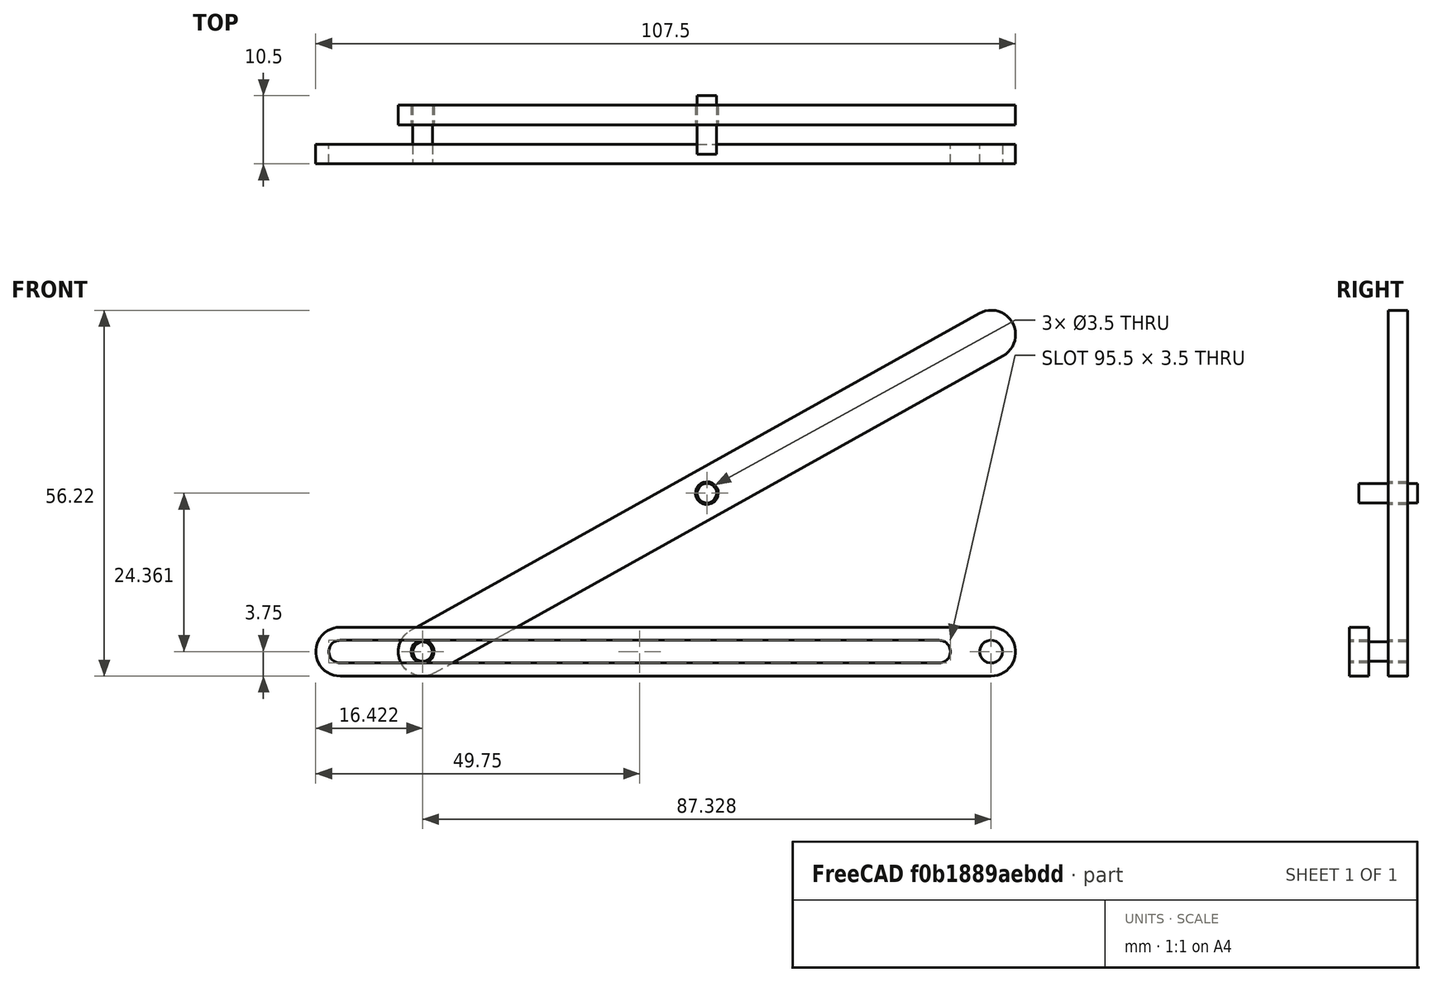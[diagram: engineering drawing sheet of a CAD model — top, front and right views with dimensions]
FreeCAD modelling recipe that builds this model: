
FCSTD DOCUMENT  (FreeCAD 1.0R38643 (Git))
Label: scissor_lift
License: All rights reserved
LicenseURL: http://en.wikipedia.org/wiki/All_rights_reserved
objects: App::FeaturePython×8, PartDesign::Body×6, Sketcher::SketchObject×3, PartDesign::Pad×3, PartDesign::FeatureBase×3, PartDesign::SubShapeBinder×1, Assembly::JointGroup×1, Assembly::AssemblyObject×1
note: 28 computed .brp shape members not serialized (recipe doc carries the construction recipe); baked Part::Feature solids carry a one-line shape summary decoded from their .brp

FEATURE [Sketcher::SketchObject] Sketch
  ArcFitTolerance = 1e-06
  AttachmentSupport = -> [XY_Plane]
  FullyConstrained = true
  MakeInternals = false
  MapMode = 5
  sketch-geometry (9):
    g0: ArcOfCircle CenterX=-50 CenterY=0 CenterZ=0 NormalX=0 NormalY=0 NormalZ=1 AngleXU=0 Radius=3.75 StartAngle=1.5708 EndAngle=4.71239
    g1: ArcOfCircle CenterX=50 CenterY=0 CenterZ=0 NormalX=0 NormalY=0 NormalZ=1 AngleXU=0 Radius=3.75 StartAngle=4.71239 EndAngle=7.85398
    g2: LineSegment StartX=-50 StartY=3.75 StartZ=0 EndX=50 EndY=3.75 EndZ=0
    g3: LineSegment StartX=-50 StartY=-3.75 StartZ=0 EndX=50 EndY=-3.75 EndZ=0
    g4: ArcOfCircle CenterX=-50 CenterY=0 CenterZ=0 NormalX=0 NormalY=0 NormalZ=1 AngleXU=0 Radius=1.75 StartAngle=1.5708 EndAngle=4.71239
    g5: ArcOfCircle CenterX=42 CenterY=1.1702e-12 CenterZ=0 NormalX=0 NormalY=0 NormalZ=1 AngleXU=0 Radius=1.75 StartAngle=4.71239 EndAngle=7.85398
    g6: LineSegment StartX=-50 StartY=1.75 StartZ=0 EndX=42 EndY=1.75 EndZ=0
    g7: LineSegment StartX=-50 StartY=-1.75 StartZ=0 EndX=42 EndY=-1.75 EndZ=0
    g8: Circle CenterX=50 CenterY=0 CenterZ=0 NormalX=0 NormalY=0 NormalZ=1 AngleXU=0 Radius=1.75
  constraints (20):
    c: Tangent(g0,g2) = 1.5708
    c: Tangent(g0,g3) = -1.5708
    c: Tangent(g1,g2) = 1.5708
    c: Tangent(g1,g3) = -1.5708
    c: Equal(g0,g1)
    c: PointOnObject(g0,g-1)
    c: Symmetric(g0,g1,g-1)
    c: DistanceX(g0,g1) = 100
    c: DistanceY(g0,g0) = 7.5
    c: Tangent(g4,g6) = 1.5708
    c: Tangent(g4,g7) = -1.5708
    c: Tangent(g5,g6) = 1.5708
    c: Tangent(g5,g7) = -1.5708
    c: Equal(g4,g5)
    c: Horizontal(g7)
    c: Coincident(g4,g0)
    c: Distance(g4,g4) = 3.5
    c: Coincident(g8,g1)
    c: Diameter(g8) = 3.5
    c: DistanceX(g5,g1) = 8
FEATURE [PartDesign::Pad] Pad
  Direction = (0,0,1)
  Length = 3
  Length2 = 10
  Profile = -> Sketch
  ReferenceAxis = -> Sketch [N_Axis]
  Suppressed = false
  Type = 0
FEATURE [PartDesign::Body] Body  label="base"
  AllowCompound = false
  Group = -> [Sketch,Pad]
  Origin = -> Origin
  Placement = pos=(0,1.5,1.5) rot=(1,0,0;1.5708rad)
  Tip = -> Pad
FEATURE [PartDesign::SubShapeBinder] Binder
  BindCopyOnChange = 0
  BindMode = 0
  ClaimChildren = false
  Context = -> Body001 [Binder.]
  Fuse = false
  MakeFace = true
  OffsetFill = false
  OffsetIntersection = false
  OffsetJoinType = 0
  OffsetOpenResult = false
  PartialLoad = false
  Relative = true
  Support = -> [Body]
  _Version = 2
FEATURE [Sketcher::SketchObject] Sketch001
  ArcFitTolerance = 1e-06
  AttachmentSupport = -> [XY_Plane001]
  ExternalGeometry = -> [Binder]
  FullyConstrained = true
  MakeInternals = false
  MapMode = 5
  sketch-geometry (6):
    g0: ArcOfCircle CenterX=-50 CenterY=-2e-16 CenterZ=0 NormalX=0 NormalY=0 NormalZ=1 AngleXU=0 Radius=3.75 StartAngle=1.5708 EndAngle=4.71239
    g1: ArcOfCircle CenterX=50 CenterY=2e-16 CenterZ=0 NormalX=0 NormalY=0 NormalZ=1 AngleXU=0 Radius=3.75 StartAngle=4.71239 EndAngle=7.85398
    g2: LineSegment StartX=-50 StartY=3.75 StartZ=0 EndX=50 EndY=3.75 EndZ=0
    g3: LineSegment StartX=-50 StartY=-3.75 StartZ=0 EndX=50 EndY=-3.75 EndZ=0
    g4: Circle CenterX=-50 CenterY=-2e-16 CenterZ=0 NormalX=0 NormalY=0 NormalZ=1 AngleXU=0 Radius=1.75
    g5: Circle CenterX=0 CenterY=0 CenterZ=0 NormalX=0 NormalY=0 NormalZ=1 AngleXU=0 Radius=1.75
  constraints (13):
    c: Tangent(g0,g2) = 1.5708
    c: Tangent(g0,g3) = -1.5708
    c: Tangent(g1,g2) = 1.5708
    c: Tangent(g1,g3) = -1.5708
    c: Equal(g0,g1)
    c: Horizontal(g2)
    c: Symmetric(g0,g1,g-1)
    c: Equal(g-3,g2)
    c: Equal(g-4,g1)
    c: Coincident(g4,g0)
    c: Equal(g4,g-5)
    c: Coincident(g5,g-1)
    c: Equal(g4,g5)
FEATURE [PartDesign::Pad] Pad001
  Direction = (0,0,1)
  Length = 3
  Length2 = 10
  Profile = -> Sketch001
  ReferenceAxis = -> Sketch001 [N_Axis]
  Suppressed = false
  Type = 0
FEATURE [PartDesign::Body] Body001  label="arm_1"
  AllowCompound = false
  Group = -> [Binder,Sketch001,Pad001]
  Origin = -> Origin001
  Placement = pos=(6.33603,1.5,25.861) rot=(0.180877,0.695443,0.695444;3.49948rad)
  Tip = -> Pad001
FEATURE [PartDesign::FeatureBase] Clone
  BaseFeature = -> Body001
  Placement = pos=(0,23.6,0) rot=(0,0,1;0rad)
  Suppressed = false
FEATURE [PartDesign::Body] Body002  label="arm_2"
  AllowCompound = false
  Group = -> [Clone]
  Origin = -> Origin002
  Placement = pos=(-5.16236,4.49999,46.4704) rot=(-0.938525,-0.2441,-0.2441;1.6342rad)
  Tip = -> Clone
FEATURE [Sketcher::SketchObject] Sketch002
  ArcFitTolerance = 1e-06
  AttachmentSupport = -> [XY_Plane003]
  FullyConstrained = true
  MakeInternals = false
  MapMode = 5
  sketch-geometry (1):
    g0: Circle CenterX=0 CenterY=0 CenterZ=0 NormalX=0 NormalY=0 NormalZ=1 AngleXU=0 Radius=1.5
  constraints (2):
    c: Coincident(g0,g-1)
    c: Diameter(g0) = 3
FEATURE [PartDesign::Pad] Pad002
  Direction = (0,0,1)
  Length = 9
  Length2 = 10
  Profile = -> Sketch002
  ReferenceAxis = -> Sketch002 [N_Axis]
  Suppressed = false
  Type = 0
FEATURE [PartDesign::Body] Body003  label="pin_1"
  AllowCompound = false
  Group = -> [Sketch002,Pad002]
  Origin = -> Origin003
  Placement = pos=(50,7.5,1.5) rot=(0.993796,-0.078645,0.078645;1.57702rad)
  Tip = -> Pad002
FEATURE [PartDesign::FeatureBase] Clone001
  BaseFeature = -> Body003
  Placement = pos=(-78.7,0,0) rot=(0,0,1;0rad)
  Suppressed = false
FEATURE [PartDesign::Body] Body004  label="pin_2"
  AllowCompound = false
  Group = -> [Clone001]
  Origin = -> Origin004
  Placement = pos=(-28.489,-1.54373e-05,96.4365) rot=(0.402424,0.647323,0.647323;3.90678rad)
  Tip = -> Clone001
FEATURE [PartDesign::FeatureBase] Clone002
  BaseFeature = -> Body003
  Placement = pos=(-78.7,0,0) rot=(0,0,1;0rad)
  Suppressed = false
FEATURE [PartDesign::Body] Body005  label="pin_3"
  AllowCompound = false
  Group = -> [Clone002]
  Origin = -> Origin005
  Placement = pos=(28.0818,-1.50001,45.2637) rot=(-0.918845,-0.279038,-0.279038;1.65533rad)
  Tip = -> Clone002
FEATURE [App::FeaturePython] GroundedJoint  # Assembly grounded joint (typed FeaturePython)
  ObjectToGround = -> Body
  Placement = pos=(0,1.5,1.5) rot=(1,0,0;1.5708rad)
FEATURE [App::FeaturePython] Revolute  # Assembly joint (typed FeaturePython)
  Activated = true
  AngleMax = 0
  AngleMin = 0
  Detach1 = false
  Detach2 = false
  Distance = 0
  Distance2 = 0
  EnableAngleMax = false
  EnableAngleMin = false
  EnableLengthMax = false
  EnableLengthMin = false
  JointType = 1 (Revolute)
  LengthMax = 0
  LengthMin = 0
  Offset = (0,0,0)
  Placement1 = pos=(0,-2.7e-15,9) rot=(0,0,1;0rad)
  Placement2 = pos=(50,0,3) rot=(0,0,1;0rad)
  Reference1 = -> Assembly [Body003.Pad002.Face1,Body003.Pad002.Edge3]
  Reference2 = -> Assembly [Body.Pad.Face9,Body.Pad.Edge3]
  Rotation = 0
FEATURE [App::FeaturePython] Cylindrical  # Assembly joint (typed FeaturePython)
  Activated = true
  AngleMax = 0
  AngleMin = 0
  Detach1 = false
  Detach2 = false
  Distance = 0
  Distance2 = 0
  EnableAngleMax = false
  EnableAngleMin = false
  EnableLengthMax = false
  EnableLengthMin = false
  JointType = 2 (Cylindrical)
  LengthMax = 0
  LengthMin = 0
  Offset = (0,0,0)
  Placement1 = pos=(0,-1.8e-15,4.5) rot=(0,0,1;0rad)
  Placement2 = pos=(-50,0,1.5) rot=(0,0,1;0rad)
  Reference1 = -> Assembly [Body003.Pad002.Face1,Body003.Pad002.Face1]
  Reference2 = -> Assembly [Body001.Pad001.Face6,Body001.Pad001.Face6]
  Rotation = 0
FEATURE [App::FeaturePython] Distance  # Assembly joint (typed FeaturePython)
  Activated = true
  AngleMax = 0
  AngleMin = 0
  Detach1 = false
  Detach2 = false
  Distance = 0
  Distance2 = 0
  EnableAngleMax = false
  EnableAngleMin = false
  EnableLengthMax = false
  EnableLengthMin = false
  JointType = 5 (Distance)
  LengthMax = 0
  LengthMin = 0
  Offset = (0,0,0)
  Placement1 = pos=(0.620769,3.6e-15,0) rot=(0,0,1;0rad)
  Placement2 = pos=(1.86655,-6.288e-13,0) rot=(0,0,1;0rad)
  Reference1 = -> Assembly [Body001.Pad001.Face7,Body001.Pad001.Vertex11]
  Reference2 = -> Assembly [Body.Pad.Face10,Body.Pad.Vertex7]
  Rotation = 0
FEATURE [App::FeaturePython] Revolute001  # Assembly joint (typed FeaturePython)
  Activated = true
  AngleMax = 0
  AngleMin = 0
  Detach1 = false
  Detach2 = false
  Distance = 0
  Distance2 = 0
  EnableAngleMax = false
  EnableAngleMin = false
  EnableLengthMax = false
  EnableLengthMin = false
  JointType = 1 (Revolute)
  LengthMax = 0
  LengthMin = 0
  Offset = (0,0,0)
  Placement1 = pos=(-78.7,7.1e-15,4.5) rot=(0,0,1;0rad)
  Placement2 = pos=(0,0,3) rot=(0,0,1;0rad)
  Reference1 = -> Assembly [Body004.Clone001.Face1,Body004.Clone001.Face1]
  Reference2 = -> Assembly [Body001.Pad001.Edge15,Body001.Pad001.Edge15]
  Rotation = 0
FEATURE [App::FeaturePython] Revolute002  # Assembly joint (typed FeaturePython)
  Activated = true
  AngleMax = 0
  AngleMin = 0
  Detach1 = false
  Detach2 = false
  Distance = 0
  Distance2 = 0
  EnableAngleMax = false
  EnableAngleMin = false
  EnableLengthMax = false
  EnableLengthMin = false
  JointType = 1 (Revolute)
  LengthMax = 0
  LengthMin = 0
  Offset = (0,0,0)
  Placement1 = pos=(0,23.6,0) rot=(0,0,1;0rad)
  Placement2 = pos=(-78.7,7.1e-15,4.5) rot=(0,0,1;0rad)
  Reference1 = -> Assembly [Body002.Clone.Edge14,Body002.Clone.Edge14]
  Reference2 = -> Assembly [Body004.Clone001.Face1,Body004.Clone001.Face1]
  Rotation = 0
FEATURE [App::FeaturePython] Revolute003  # Assembly joint (typed FeaturePython)
  Activated = true
  AngleMax = 0
  AngleMin = 0
  Detach1 = false
  Detach2 = false
  Distance = 0
  Distance2 = 0
  EnableAngleMax = false
  EnableAngleMin = false
  EnableLengthMax = false
  EnableLengthMin = false
  JointType = 1 (Revolute)
  LengthMax = 0
  LengthMin = 0
  Offset = (0,0,0)
  Placement1 = pos=(-78.7,2.49e-14,9) rot=(0,0,1;0rad)
  Placement2 = pos=(-50,23.6,3) rot=(0,0,1;0rad)
  Reference1 = -> Assembly [Body005.Clone002.Edge3,Body005.Clone002.Edge3]
  Reference2 = -> Assembly [Body002.Clone.Edge18,Body002.Clone.Edge18]
  Rotation = 0
FEATURE [App::FeaturePython] Distance001  # Assembly joint (typed FeaturePython)
  Activated = true
  AngleMax = 0
  AngleMin = 0
  Detach1 = false
  Detach2 = false
  Distance = 0.25
  Distance2 = 0
  EnableAngleMax = false
  EnableAngleMin = false
  EnableLengthMax = false
  EnableLengthMin = false
  JointType = 5 (Distance)
  LengthMax = 0
  LengthMin = 0
  Offset = (0,0,0)
  Placement1 = pos=(-4,-1.75,1.5) rot=(-1,0,0;1.5708rad)
  Placement2 = pos=(-78.7,2.13e-14,4.5) rot=(0,0,1;0rad)
  Reference1 = -> Assembly [Body.Pad.Face6,Body.Pad.Vertex11]
  Reference2 = -> Assembly [Body005.Clone002.Face1,Body005.Clone002.Edge2]
  Rotation = 0
FEATURE [Assembly::JointGroup] Joints
  Group = -> [GroundedJoint,Revolute,Cylindrical,Distance,Revolute001,Revolute002,Revolute003,Distance001]
FEATURE [Assembly::AssemblyObject] Assembly
  Group = -> [Joints,Body,Body001,Body002,Body003,Body004,Body005,GroundedJoint,Revolute,Cylindrical,Distance,Revolute001,Revolute002,Revolute003,Distance001]
  Origin = -> Origin006
  Type = Assembly
